FCSTD DOCUMENT  (FreeCAD 1.0R39319 (Git))
Label: 01_assembly_frame
License: All rights reserved
LicenseURL: http://en.wikipedia.org/wiki/All_rights_reserved
objects: App::Link×7, App::FeaturePython×7, Assembly::JointGroup×1, Assembly::AssemblyObject×1
EXTERNAL_REF file=02_frame_15_x_30.FCStd obj=Body
EXTERNAL_REF file=03_frame_sleeve.FCStd obj=Body

FEATURE [App::Link] Body
  LinkedObject = -> <external 02_frame_15_x_30.FCStd>#Body
FEATURE [App::FeaturePython] GroundedJoint  # Assembly grounded joint (typed FeaturePython)
  ObjectToGround = -> Body
FEATURE [App::Link] Body001
  LinkPlacement = pos=(230,-210,15) rot=(1,0,0;1.5708rad)
  LinkedObject = -> <external 03_frame_sleeve.FCStd>#Body
  Placement = pos=(230,-210,15) rot=(1,0,0;1.5708rad)
FEATURE [App::Link] Body002
  LinkPlacement = pos=(138,-210,15) rot=(1,0,0;1.5708rad)
  LinkedObject = -> <external 03_frame_sleeve.FCStd>#Body
  Placement = pos=(138,-210,15) rot=(1,0,0;1.5708rad)
FEATURE [App::Link] Body003
  LinkPlacement = pos=(46,-210,15) rot=(1,0,0;1.5708rad)
  LinkedObject = -> <external 03_frame_sleeve.FCStd>#Body
  Placement = pos=(46,-210,15) rot=(1,0,0;1.5708rad)
FEATURE [App::Link] Body004
  LinkPlacement = pos=(-46,-210,15) rot=(1,0,0;1.5708rad)
  LinkedObject = -> <external 03_frame_sleeve.FCStd>#Body
  Placement = pos=(-46,-210,15) rot=(1,0,0;1.5708rad)
FEATURE [App::Link] Body005
  LinkPlacement = pos=(-138,-210,15) rot=(1,0,0;1.5708rad)
  LinkedObject = -> <external 03_frame_sleeve.FCStd>#Body
  Placement = pos=(-138,-210,15) rot=(1,0,0;1.5708rad)
FEATURE [App::Link] Body006
  LinkPlacement = pos=(-230,-210,15) rot=(1,0,0;1.5708rad)
  LinkedObject = -> <external 03_frame_sleeve.FCStd>#Body
  Placement = pos=(-230,-210,15) rot=(1,0,0;1.5708rad)
FEATURE [App::FeaturePython] Joint  label="Revolute"  # Assembly joint (typed FeaturePython)
  Activated = true
  AngleMax = 0
  AngleMin = 0
  Detach1 = false
  Detach2 = false
  Distance = 0
  Distance2 = 0
  EnableAngleMax = false
  EnableAngleMin = false
  EnableLengthMax = false
  EnableLengthMin = false
  JointType = 1 (Revolute)
  LengthMax = 0
  LengthMin = 0
  Placement1 = pos=(0,0,15) rot=(0,0,1;0rad)
  Placement2 = pos=(0,-225,0) rot=(0.707107,0,0.707107;3.14159rad)
  Reference1 = -> Assembly [Body006.Edge3,Body006.Edge3]
  Reference2 = -> Assembly [Body.Edge26,Body.Edge26]
FEATURE [App::FeaturePython] Joint001  label="Revolute001"  # Assembly joint (typed FeaturePython)
  Activated = true
  AngleMax = 0
  AngleMin = 0
  Detach1 = false
  Detach2 = false
  Distance = 0
  Distance2 = 0
  EnableAngleMax = false
  EnableAngleMin = false
  EnableLengthMax = false
  EnableLengthMin = false
  JointType = 1 (Revolute)
  LengthMax = 0
  LengthMin = 0
  Placement1 = pos=(0,0,15) rot=(0,0,1;0rad)
  Placement2 = pos=(-289.5,-15,0) rot=(-0.707107,0,0.707107;3.14159rad)
  Reference1 = -> Assembly [Body005.Edge3,Body005.Edge3]
  Reference2 = -> Assembly [Body.Edge27,Body.Edge27]
FEATURE [App::FeaturePython] Joint002  label="Revolute002"  # Assembly joint (typed FeaturePython)
  Activated = true
  AngleMax = 0
  AngleMin = 0
  Detach1 = false
  Detach2 = false
  Distance = 0
  Distance2 = 0
  EnableAngleMax = false
  EnableAngleMin = false
  EnableLengthMax = false
  EnableLengthMin = false
  JointType = 1 (Revolute)
  LengthMax = 0
  LengthMin = 0
  Placement1 = pos=(0,0,15) rot=(0,0,1;0rad)
  Placement2 = pos=(0,-210,0) rot=(0.707107,0,0.707107;3.14159rad)
  Reference1 = -> Assembly [Body004.Edge3,Body004.Edge3]
  Reference2 = -> Assembly [Body.Edge28,Body.Edge28]
FEATURE [App::FeaturePython] Joint003  label="Revolute003"  # Assembly joint (typed FeaturePython)
  Activated = true
  AngleMax = 0
  AngleMin = 0
  Detach1 = false
  Detach2 = false
  Distance = 0
  Distance2 = 0
  EnableAngleMax = false
  EnableAngleMin = false
  EnableLengthMax = false
  EnableLengthMin = false
  JointType = 1 (Revolute)
  LengthMax = 0
  LengthMin = 0
  Placement1 = pos=(0,0,15) rot=(0,0,1;0rad)
  Placement2 = pos=(282,0,0) rot=(0.57735,0.57735,0.57735;4.18879rad)
  Reference1 = -> Assembly [Body003.Edge3,Body003.Edge3]
  Reference2 = -> Assembly [Body.Edge29,Body.Edge29]
FEATURE [App::FeaturePython] Joint004  label="Revolute004"  # Assembly joint (typed FeaturePython)
  Activated = true
  AngleMax = 0
  AngleMin = 0
  Detach1 = false
  Detach2 = false
  Distance = 0
  Distance2 = 0
  EnableAngleMax = false
  EnableAngleMin = false
  EnableLengthMax = false
  EnableLengthMin = false
  JointType = 1 (Revolute)
  LengthMax = 0
  LengthMin = 0
  Placement1 = pos=(0,0,15) rot=(0,0,1;0rad)
  Placement2 = pos=(0,210,0) rot=(-0.707107,0,0.707107;3.14159rad)
  Reference1 = -> Assembly [Body002.Edge3,Body002.Edge3]
  Reference2 = -> Assembly [Body.Edge30,Body.Edge30]
FEATURE [App::FeaturePython] Joint005  label="Revolute005"  # Assembly joint (typed FeaturePython)
  Activated = true
  AngleMax = 0
  AngleMin = 0
  Detach1 = false
  Detach2 = false
  Distance = 0
  Distance2 = 0
  EnableAngleMax = false
  EnableAngleMin = false
  EnableLengthMax = false
  EnableLengthMin = false
  JointType = 1 (Revolute)
  LengthMax = 0
  LengthMin = 0
  Placement1 = pos=(0,0,15) rot=(0,0,1;0rad)
  Placement2 = pos=(-289.5,15,0) rot=(-0.707107,0,0.707107;3.14159rad)
  Reference1 = -> Assembly [Body001.Edge3,Body001.Edge3]
  Reference2 = -> Assembly [Body.Edge31,Body.Edge31]
FEATURE [Assembly::JointGroup] Joints
  Group = -> [GroundedJoint,Joint,Joint001,Joint002,Joint003,Joint004,Joint005]
FEATURE [Assembly::AssemblyObject] Assembly
  Group = -> [Joints,Body,GroundedJoint,Body001,Body002,Body003,Body004,Body005,Body006,Joint,Joint001,Joint002,Joint003,Joint004,Joint005]
  Origin = -> Origin
  Type = Assembly

RESOLVED EXTERNAL PARTS (link-assembly join: the EXTERNAL_REF files above that resolve inside this repo's crawl, each included once):
---- part 02_frame_15_x_30.FCStd = doc fcstd_6e40d2458701 ----
FCSTD DOCUMENT  (FreeCAD 1.0R39319 (Git))
Label: 02_frame_15_x_30
License: All rights reserved
LicenseURL: http://en.wikipedia.org/wiki/All_rights_reserved
objects: TechDraw::DrawViewDimension×20, TechDraw::DrawViewBalloon×9, Sketcher::SketchObject×5, TechDraw::DrawProjGroupItem×5, PartDesign::Pocket×4, TechDraw::DrawViewAnnotation×2, Spreadsheet::Sheet×1, PartDesign::Pad×1, PartDesign::Chamfer×1, PartDesign::Body×1, TechDraw::DrawSVGTemplate×1, TechDraw::DrawProjGroup×1, TechDraw::DrawPage×1
note: 59 computed .brp shape members not serialized (recipe doc carries the construction recipe); baked Part::Feature solids carry a one-line shape summary decoded from their .brp

FEATURE [Sketcher::SketchObject] Sketch
  ArcFitTolerance = 1e-06
  AttachmentSupport = -> [XY_Plane]
  FullyConstrained = true
  MakeInternals = false
  MapMode = 5
  expr: Constraints[22] = Spreadsheet.height_outside
  expr: Constraints[23] = Spreadsheet.lenght_outside
  expr: Constraints[24] = Spreadsheet.lenght_outside - 2 * Spreadsheet.height_frame
  expr: Constraints[25] = Spreadsheet.height_outside - 2 * Spreadsheet.height_frame
  sketch-geometry (10):
    g0: LineSegment StartX=-282 StartY=210 StartZ=0 EndX=-282 EndY=-210 EndZ=0
    g1: LineSegment StartX=-282 StartY=-210 StartZ=0 EndX=282 EndY=-210 EndZ=0
    g2: LineSegment StartX=282 StartY=-210 StartZ=0 EndX=282 EndY=210 EndZ=0
    g3: LineSegment StartX=282 StartY=210 StartZ=0 EndX=-282 EndY=210 EndZ=0
    g4: LineSegment [constr] StartX=-282 StartY=210 StartZ=0 EndX=282 EndY=-210 EndZ=0
    g5: LineSegment StartX=-297 StartY=225 StartZ=0 EndX=-297 EndY=-225 EndZ=0
    g6: LineSegment StartX=-297 StartY=-225 StartZ=0 EndX=297 EndY=-225 EndZ=0
    g7: LineSegment StartX=297 StartY=-225 StartZ=0 EndX=297 EndY=225 EndZ=0
    g8: LineSegment StartX=297 StartY=225 StartZ=0 EndX=-297 EndY=225 EndZ=0
    g9: LineSegment [constr] StartX=-297 StartY=225 StartZ=0 EndX=297 EndY=-225 EndZ=0
  constraints (26):
    c: Coincident(g0,g1)
    c: Coincident(g1,g2)
    c: Coincident(g2,g3)
    c: Coincident(g3,g0)
    c: Vertical(g0)
    c: Vertical(g2)
    c: Horizontal(g1)
    c: Horizontal(g3)
    c: Coincident(g4,g0)
    c: Coincident(g4,g1)
    c: Symmetric(g0,g1,g-1)
    c: Coincident(g5,g6)
    c: Coincident(g6,g7)
    c: Coincident(g7,g8)
    c: Coincident(g8,g5)
    c: Vertical(g5)
    c: Vertical(g7)
    c: Horizontal(g6)
    c: Horizontal(g8)
    c: Coincident(g9,g5)
    c: Coincident(g9,g6)
    c: Symmetric(g5,g6,g-1)
    c: DistanceY(g5,g5) = 450
    c: DistanceX(g8,g8) = 594
    c: DistanceX(g3,g3) = 564
    c: DistanceY(g0,g0) = 420
FEATURE [Spreadsheet::Sheet] Spreadsheet
  cells = A2='lenght_outside; B2(lenght_outside)=594; A3='height_outside; B3(height_outside)=450; A5='width_frame; B5(width_frame)=30; A6='height_frame; B6(height_frame)=15; A7='drill_size; B7(drillsize)=81
FEATURE [PartDesign::Pad] Pad
  Direction = (0,0,1)
  Length = 30
  Length2 = 10
  Profile = -> Sketch
  ReferenceAxis = -> Sketch [N_Axis]
  Suppressed = false
  Type = 0
  expr: Length = Spreadsheet.width_frame
FEATURE [Sketcher::SketchObject] Sketch001
  ArcFitTolerance = 1e-06
  AttachmentSupport = -> [YZ_Plane]
  FullyConstrained = true
  MakeInternals = false
  MapMode = 5
  Placement = pos=(0,0,0) rot=(0.57735,0.57735,0.57735;2.0944rad)
  sketch-geometry (4):
    g0: LineSegment StartX=-15 StartY=13 StartZ=0 EndX=-15 EndY=0 EndZ=0
    g1: LineSegment StartX=-15 StartY=0 StartZ=0 EndX=15 EndY=0 EndZ=0
    g2: LineSegment StartX=15 StartY=0 StartZ=0 EndX=15 EndY=13 EndZ=0
    g3: LineSegment StartX=15 StartY=13 StartZ=0 EndX=-15 EndY=13 EndZ=0
  constraints (11):
    c: Coincident(g0,g1)
    c: Coincident(g1,g2)
    c: Coincident(g2,g3)
    c: Coincident(g3,g0)
    c: Vertical(g0)
    c: Vertical(g2)
    c: Horizontal(g1)
    c: Symmetric(g0,g2,g-2)
    c: Horizontal(g1,g-1)
    c: DistanceX(g3,g3) = 30
    c: DistanceY(g0,g0) = 13
FEATURE [PartDesign::Pocket] Pocket
  BaseFeature = -> Pad
  Direction = (-1,0,0)
  Length = 594
  Length2 = 5
  Profile = -> Sketch001
  ReferenceAxis = -> Sketch001 [N_Axis]
  Suppressed = false
  Type = 0
  expr: Length = Spreadsheet.lenght_outside
FEATURE [Sketcher::SketchObject] Sketch002
  ArcFitTolerance = 1e-06
  AttachmentSupport = -> [XZ_Plane]
  ExternalGeometry = -> [Pocket]
  FullyConstrained = true
  MakeInternals = false
  MapMode = 5
  Placement = pos=(0,0,0) rot=(1,0,0;1.5708rad)
  sketch-geometry (7):
    g0: LineSegment [constr] StartX=-282 StartY=15 StartZ=0 EndX=282 EndY=15 EndZ=0
    g1: Circle CenterX=-230 CenterY=15 CenterZ=0 NormalX=0 NormalY=0 NormalZ=1 AngleXU=0 Radius=5
    g2: Circle CenterX=-138 CenterY=15 CenterZ=0 NormalX=0 NormalY=0 NormalZ=1 AngleXU=0 Radius=5
    g3: Circle CenterX=-46 CenterY=15 CenterZ=0 NormalX=0 NormalY=0 NormalZ=1 AngleXU=0 Radius=5
    g4: Circle CenterX=46 CenterY=15 CenterZ=0 NormalX=0 NormalY=0 NormalZ=1 AngleXU=0 Radius=5
    g5: Circle CenterX=138 CenterY=15 CenterZ=0 NormalX=0 NormalY=0 NormalZ=1 AngleXU=0 Radius=5
    g6: Circle CenterX=230 CenterY=15 CenterZ=0 NormalX=0 NormalY=0 NormalZ=1 AngleXU=0 Radius=5
  constraints (23):
    c: Symmetric(g-5,g-5,g0)
    c: Symmetric(g-6,g-6,g0)
    c: DistanceX(g-3,g-3) = 564
    c: PointOnObject(g1,g0)
    c: Diameter(g1) = 10
    c: PointOnObject(g2,g0)
    c: PointOnObject(g3,g0)
    c: PointOnObject(g4,g0)
    c: PointOnObject(g5,g0)
    c: Equal(g1,g2)
    c: Equal(g1,g3)
    c: Equal(g1,g4)
    c: Equal(g5,g1)
    c: PointOnObject(g6,g0)
    c: Equal(g1,g6)
    c: DistanceX(g0,g1) = 52
    c: DistanceX(g6,g0) = 52
    c: DistanceX(g1,g6) = 460
    c: DistanceX(g1,g2) = 92
    c: DistanceX(g2,g3) = 92
    c: DistanceX(g3,g4) = 92
    c: DistanceX(g4,g5) = 92
    c: DistanceX(g5,g6) = 92
FEATURE [PartDesign::Pocket] Pocket001
  BaseFeature = -> Pocket
  Direction = (0,1,-2e-16)
  Length = 225
  Length2 = 5
  Profile = -> Sketch002
  ReferenceAxis = -> Sketch002 [N_Axis]
  Reversed = true
  Suppressed = false
  Type = 0
  expr: Length = Spreadsheet.height_outside / 2
FEATURE [Sketcher::SketchObject] Sketch003
  ArcFitTolerance = 1e-06
  AttachmentSupport = -> [XZ_Plane]
  ExternalGeometry = -> [Pocket001]
  FullyConstrained = true
  MakeInternals = false
  MapMode = 5
  Placement = pos=(0,0,0) rot=(1,0,0;1.5708rad)
  sketch-geometry (7):
    g0: LineSegment [constr] StartX=-282 StartY=15 StartZ=0 EndX=282 EndY=15 EndZ=0
    g1: Circle CenterX=-230 CenterY=15 CenterZ=0 NormalX=0 NormalY=0 NormalZ=1 AngleXU=0 Radius=2.05
    g2: Circle CenterX=-138 CenterY=15 CenterZ=0 NormalX=0 NormalY=0 NormalZ=1 AngleXU=0 Radius=2.05
    g3: Circle CenterX=-46 CenterY=15 CenterZ=0 NormalX=0 NormalY=0 NormalZ=1 AngleXU=0 Radius=2.05
    g4: Circle CenterX=46 CenterY=15 CenterZ=0 NormalX=0 NormalY=0 NormalZ=1 AngleXU=0 Radius=2.05
    g5: Circle CenterX=138 CenterY=15 CenterZ=0 NormalX=0 NormalY=0 NormalZ=1 AngleXU=0 Radius=2.05
    g6: Circle CenterX=230 CenterY=15 CenterZ=0 NormalX=0 NormalY=0 NormalZ=1 AngleXU=0 Radius=2.05
  constraints (22):
    c: Horizontal(g0)
    c: PointOnObject(g0,g-4)
    c: Symmetric(g-3,g-3,g0)
    c: PointOnObject(g1,g0)
    c: Distance(g1,g-3) = 52
    c: Diameter(g1) = 4.1
    c: PointOnObject(g2,g0)
    c: DistanceX(g1,g2) = 92
    c: Equal(g1,g2)
    c: PointOnObject(g3,g0)
    c: Equal(g2,g3)
    c: PointOnObject(g4,g0)
    c: PointOnObject(g5,g0)
    c: Equal(g1,g4)
    c: Equal(g1,g5)
    c: DistanceX(g2,g3) = 92
    c: DistanceX(g3,g4) = 92
    c: DistanceX(g4,g5) = 92
    c: PointOnObject(g6,g0)
    c: Equal(g1,g6)
    c: DistanceX(g5,g6) = 92
    c: DistanceX(g6,g0) = 52
FEATURE [PartDesign::Pocket] Pocket002
  BaseFeature = -> Pocket001
  Direction = (0,1,-2e-16)
  Length = 218
  Length2 = 5
  Profile = -> Sketch003
  ReferenceAxis = -> Sketch003 [N_Axis]
  Suppressed = false
  Type = 0
  expr: Length = Spreadsheet.height_outside / 2 - 7
FEATURE [Sketcher::SketchObject] Sketch004
  ArcFitTolerance = 1e-06
  AttachmentSupport = -> [YZ_Plane]
  ExternalGeometry = -> [Pocket002]
  FullyConstrained = true
  MakeInternals = false
  MapMode = 5
  Placement = pos=(0,0,0) rot=(0.57735,0.57735,0.57735;2.0944rad)
  sketch-geometry (3):
    g0: LineSegment [constr] StartX=-210 StartY=15 StartZ=0 EndX=210 EndY=15 EndZ=0
    g1: Circle CenterX=-170 CenterY=15 CenterZ=0 NormalX=0 NormalY=0 NormalZ=1 AngleXU=0 Radius=2.5
    g2: Circle CenterX=170 CenterY=15 CenterZ=0 NormalX=0 NormalY=0 NormalZ=1 AngleXU=0 Radius=2.5
  constraints (8):
    c: Symmetric(g-3,g-3,g0)
    c: Symmetric(g-4,g-4,g0)
    c: PointOnObject(g1,g0)
    c: PointOnObject(g2,g0)
    c: Distance(g1,g-3) = 40
    c: Distance(g0,g2) = 40
    c: Diameter(g1) = 5
    c: Equal(g1,g2)
FEATURE [PartDesign::Pocket] Pocket003
  BaseFeature = -> Pocket002
  Direction = (-1,0,0)
  Length = 5
  Length2 = 5
  Midplane = true
  Profile = -> Sketch004
  ReferenceAxis = -> Sketch004 [N_Axis]
  Suppressed = false
  Type = 1
FEATURE [PartDesign::Chamfer] Chamfer
  Angle = 45
  Base = -> Pocket003 [Edge41,Edge43,Edge57,Edge58]
  BaseFeature = -> Pocket003
  ChamferType = 0
  FlipDirection = false
  Size = 5
  Size2 = 1
  SupportTransform = false
  Suppressed = false
  UseAllEdges = false
FEATURE [PartDesign::Body] Body
  AllowCompound = false
  Group = -> [Sketch,Pad,Sketch001,Pocket,Sketch002,Pocket001,Sketch003,Pocket002,Sketch004,Pocket003,Chamfer]
  Origin = -> Origin
  Tip = -> Chamfer
FEATURE [TechDraw::DrawSVGTemplate] Template
  EditableTexts = AuthorName=Matthias Mosimann; CheckDate=N/A; CreationDate=15/04/2026; DrawingNumber=1.0; FC-Title=Rahmen; SheetNumber=1 / 1; SupervisorName=N/A; Weight=WEIGHT; scale=1 : 5
  Height = 297
  Orientation = 1
  Template = C:/Program Files/FreeCAD 1.0/data/Mod/TechDraw/Templates/A3_Landscape_TD.svg
  Width = 420
FEATURE [TechDraw::DrawProjGroupItem] View  label="Front"
  CoarseView = false
  Direction = (0,-1,0)
  Focus = 100
  HardHidden = false
  IsoCount = 0
  IsoHidden = false
  IsoVisible = false
  LockPosition = true
  Perspective = false
  Rotation = 0
  RotationVector = (1,0,0)
  Scale = 0.2
  ScaleType = 2
  ScrubCount = 1
  SeamHidden = false
  SeamVisible = true
  SmoothHidden = false
  SmoothVisible = true
  Source = -> [Body]
  Type = 0
  X = 0
  XDirection = (-1,0,-1e-16)
  Y = 0
FEATURE [TechDraw::DrawProjGroupItem] ProjItem  label="Right"
  CoarseView = false
  Direction = (-1,-1e-16,-1e-16)
  Focus = 100
  HardHidden = false
  IsoCount = 0
  IsoHidden = false
  IsoVisible = false
  LockPosition = true
  Perspective = false
  Rotation = 0
  RotationVector = (1,0,0)
  Scale = 0.2
  ScaleType = 2
  ScrubCount = 1
  SeamHidden = false
  SeamVisible = true
  SmoothHidden = false
  SmoothVisible = true
  Source = -> [Body]
  Type = 2
  X = -119.062
  XDirection = (-1e-16,1,0)
  Y = 0
FEATURE [TechDraw::DrawProjGroupItem] ProjItem002  label="Top"
  CoarseView = false
  Direction = (1e-16,0,-1)
  Focus = 100
  HardHidden = true
  IsoCount = 0
  IsoHidden = false
  IsoVisible = false
  LockPosition = true
  Perspective = false
  Rotation = 0
  RotationVector = (1,0,0)
  Scale = 0.2
  ScaleType = 2
  ScrubCount = 1
  SeamHidden = false
  SeamVisible = true
  SmoothHidden = false
  SmoothVisible = true
  Source = -> [Body]
  Type = 4
  X = 0
  XDirection = (-1,0,-1e-16)
  Y = -80.6268
FEATURE [TechDraw::DrawProjGroupItem] ProjItem003  label="Left"
  CoarseView = false
  Direction = (1,-1e-16,1e-16)
  Focus = 100
  HardHidden = false
  IsoCount = 0
  IsoHidden = false
  IsoVisible = false
  LockPosition = true
  Perspective = false
  Rotation = 0
  RotationVector = (1,0,0)
  Scale = 0.2
  ScaleType = 2
  ScrubCount = 1
  SeamHidden = false
  SeamVisible = true
  SmoothHidden = false
  SmoothVisible = true
  Source = -> [Body]
  Type = 1
  X = 121.888
  XDirection = (-1e-16,-1,0)
  Y = 0
FEATURE [TechDraw::DrawProjGroupItem] ProjItem004  label="FrontTopLeft"
  CoarseView = false
  Direction = (0.57735,-0.57735,-0.57735)
  Focus = 100
  HardHidden = false
  IsoCount = 0
  IsoHidden = false
  IsoVisible = false
  LockPosition = true
  Perspective = false
  Rotation = 0
  RotationVector = (1,0,0)
  Scale = 0.2
  ScaleType = 2
  ScrubCount = 1
  SeamHidden = false
  SeamVisible = true
  SmoothHidden = false
  SmoothVisible = true
  Source = -> [Body]
  Type = 6
  X = 147.596
  XDirection = (-0.707107,-0.707107,-1e-16)
  Y = -76.8368
FEATURE [TechDraw::DrawProjGroup] ProjGroup
  Anchor = -> View
  AutoDistribute = true
  LockPosition = false
  ProjectionType = 0
  Rotation = 0
  Scale = 0.2
  ScaleType = 2
  Source = -> [Body]
  Views = -> [View,ProjItem,ProjItem002,ProjItem003,ProjItem004]
  X = 185.522
  Y = 222.445
  spacingX = 15
  spacingY = 15
FEATURE [TechDraw::DrawViewDimension] Dimension
  AngleOverride = false
  Arbitrary = false
  ArbitraryTolerances = false
  BoxCorners = (2) [(-59.4,-45,0),(59.4,45,0)]
  EqualTolerance = true
  ExtensionAngle = 0
  FormatSpec = %.2w
  FormatSpecOverTolerance = %+.2w
  FormatSpecUnderTolerance = %+.2w
  Inverted = false
  LineAngle = 0
  LockPosition = false
  MeasureType = 1
  OverTolerance = 0
  References2D = -> [ProjItem002]
  Rotation = 0
  ScaleType = 0
  TheoreticalExact = false
  Type = 2
  UnderTolerance = 0
  X = -72.114
  Y = 5.93997
FEATURE [TechDraw::DrawViewDimension] Dimension001
  AngleOverride = false
  Arbitrary = false
  ArbitraryTolerances = false
  BoxCorners = (2) [(-59.4,-45,0),(59.4,45,0)]
  EqualTolerance = true
  ExtensionAngle = 0
  FormatSpec = %.2w
  FormatSpecOverTolerance = %+.2w
  FormatSpecUnderTolerance = %+.2w
  Inverted = false
  LineAngle = 0
  LockPosition = false
  MeasureType = 1
  OverTolerance = 0
  References2D = -> [ProjItem002]
  Rotation = 0
  ScaleType = 0
  TheoreticalExact = false
  Type = 1
  UnderTolerance = 0
  X = 0
  Y = 61.892
FEATURE [TechDraw::DrawViewDimension] Dimension002
  AngleOverride = false
  Arbitrary = false
  ArbitraryTolerances = false
  BoxCorners = (2) [(-45,-3,0),(45,3,0)]
  EqualTolerance = true
  ExtensionAngle = 0
  FormatSpec = %.2w
  FormatSpecOverTolerance = %+.2w
  FormatSpecUnderTolerance = %+.2w
  Inverted = false
  LineAngle = 0
  LockPosition = false
  MeasureType = 1
  OverTolerance = 0
  References2D = -> [ProjItem]
  Rotation = 0
  ScaleType = 0
  TheoreticalExact = false
  Type = 0
  UnderTolerance = 0
  X = -39.5
  Y = -15.8335
FEATURE [TechDraw::DrawViewDimension] Dimension003
  AngleOverride = false
  Arbitrary = false
  ArbitraryTolerances = false
  BoxCorners = (2) [(-45,-3,0),(45,3,0)]
  EqualTolerance = true
  ExtensionAngle = 0
  FormatSpec = ⌀%.2w
  FormatSpecOverTolerance = %+.2w
  FormatSpecUnderTolerance = %+.2w
  Inverted = false
  LineAngle = 0
  LockPosition = false
  MeasureType = 1
  OverTolerance = 0
  References2D = -> [ProjItem]
  Rotation = 0
  ScaleType = 0
  TheoreticalExact = false
  Type = 5
  UnderTolerance = 0
  X = -30.7122
  Y = 14.8466
FEATURE [TechDraw::DrawViewDimension] Dimension004
  AngleOverride = false
  Arbitrary = false
  ArbitraryTolerances = false
  BoxCorners = (2) [(-45,-3,0),(45,3,0)]
  EqualTolerance = true
  ExtensionAngle = 0
  FormatSpec = %.2w
  FormatSpecOverTolerance = %+.2w
  FormatSpecUnderTolerance = %+.2w
  Inverted = false
  LineAngle = 0
  LockPosition = false
  MeasureType = 1
  OverTolerance = 0
  References2D = -> [ProjItem]
  Rotation = 0
  ScaleType = 0
  TheoreticalExact = false
  Type = 0
  UnderTolerance = 0
  X = 39.5
  Y = -15.8335
FEATURE [TechDraw::DrawViewDimension] Dimension005
  AngleOverride = false
  Arbitrary = false
  ArbitraryTolerances = false
  BoxCorners = (2) [(-45,-3,0),(45,3,0)]
  EqualTolerance = true
  ExtensionAngle = 0
  FormatSpec = ⌀%.2w
  FormatSpecOverTolerance = %+.2w
  FormatSpecUnderTolerance = %+.2w
  Inverted = false
  LineAngle = 0
  LockPosition = false
  MeasureType = 1
  OverTolerance = 0
  References2D = -> [ProjItem]
  Rotation = 0
  ScaleType = 0
  TheoreticalExact = false
  Type = 5
  UnderTolerance = 0
  X = 38.1595
  Y = 15.5364
FEATURE [TechDraw::DrawViewDimension] Dimension006
  AngleOverride = false
  Arbitrary = false
  ArbitraryTolerances = false
  BoxCorners = (2) [(-45,-3,0),(45,3,0)]
  EqualTolerance = true
  ExtensionAngle = 0
  FormatSpec = %.2w
  FormatSpecOverTolerance = %+.2w
  FormatSpecUnderTolerance = %+.2w
  Inverted = false
  LineAngle = 0
  LockPosition = false
  MeasureType = 1
  OverTolerance = 0
  References2D = -> [ProjItem]
  Rotation = 0
  ScaleType = 0
  TheoreticalExact = false
  Type = 0
  UnderTolerance = 0
  X = -13.9563
  Y = 10.1442
FEATURE [TechDraw::DrawViewDimension] Dimension007
  AngleOverride = false
  Arbitrary = false
  ArbitraryTolerances = false
  BoxCorners = (2) [(-45,-3,0),(45,3,0)]
  EqualTolerance = true
  ExtensionAngle = 0
  FormatSpec = %.2w
  FormatSpecOverTolerance = %+.2w
  FormatSpecUnderTolerance = %+.2w
  Inverted = false
  LineAngle = 0
  LockPosition = false
  MeasureType = 1
  OverTolerance = 0
  References2D = -> [ProjItem]
  Rotation = 0
  ScaleType = 0
  TheoreticalExact = false
  Type = 0
  UnderTolerance = 0
  X = -17.7771
  Y = 24.7768
FEATURE [TechDraw::DrawViewDimension] Dimension008
  AngleOverride = false
  Arbitrary = false
  ArbitraryTolerances = false
  BoxCorners = (2) [(-59.4,-3,0),(59.4,3,0)]
  EqualTolerance = true
  ExtensionAngle = 0
  FormatSpec = %.2w
  FormatSpecOverTolerance = %+.2w
  FormatSpecUnderTolerance = %+.2w
  Inverted = false
  LineAngle = 0
  LockPosition = false
  MeasureType = 1
  OverTolerance = 0
  References2D = -> [View]
  Rotation = 0
  ScaleType = 0
  TheoreticalExact = false
  Type = 0
  UnderTolerance = 0
  X = -52.7
  Y = 22.4873
FEATURE [TechDraw::DrawViewDimension] Dimension009
  AngleOverride = false
  Arbitrary = false
  ArbitraryTolerances = false
  BoxCorners = (2) [(-59.4,-3,0),(59.4,3,0)]
  EqualTolerance = true
  ExtensionAngle = 0
  FormatSpec = %.2w
  FormatSpecOverTolerance = %+.2w
  FormatSpecUnderTolerance = %+.2w
  Inverted = false
  LineAngle = 0
  LockPosition = false
  MeasureType = 1
  OverTolerance = 0
  References2D = -> [View]
  Rotation = 0
  ScaleType = 0
  TheoreticalExact = false
  Type = 1
  UnderTolerance = 0
  X = -36.8
  Y = 22.4873
FEATURE [TechDraw::DrawViewDimension] Dimension010
  AngleOverride = false
  Arbitrary = false
  ArbitraryTolerances = false
  BoxCorners = (2) [(-59.4,-3,0),(59.4,3,0)]
  EqualTolerance = true
  ExtensionAngle = 0
  FormatSpec = %.2w
  FormatSpecOverTolerance = %+.2w
  FormatSpecUnderTolerance = %+.2w
  Inverted = false
  LineAngle = 0
  LockPosition = false
  MeasureType = 1
  OverTolerance = 0
  References2D = -> [View]
  Rotation = 0
  ScaleType = 0
  TheoreticalExact = false
  Type = 2
  UnderTolerance = 0
  X = 65.2162
  Y = 0
FEATURE [TechDraw::DrawViewDimension] Dimension011
  AngleOverride = false
  Arbitrary = false
  ArbitraryTolerances = false
  BoxCorners = (2) [(-59.4,-45,0),(59.4,45,0)]
  EqualTolerance = true
  ExtensionAngle = 0
  FormatSpec = %.2w
  FormatSpecOverTolerance = %+.2w
  FormatSpecUnderTolerance = %+.2w
  Inverted = false
  LineAngle = 0
  LockPosition = false
  MeasureType = 1
  OverTolerance = 0
  References2D = -> [ProjItem002]
  Rotation = 0
  ScaleType = 0
  TheoreticalExact = false
  Type = 0
  UnderTolerance = 0
  X = 62.2692
  Y = 54.4773
FEATURE [TechDraw::DrawViewDimension] Dimension012
  AngleOverride = false
  Arbitrary = false
  ArbitraryTolerances = false
  BoxCorners = (2) [(-59.4,-3,0),(59.4,3,0)]
  EqualTolerance = true
  ExtensionAngle = 0
  FormatSpec = %.2w
  FormatSpecOverTolerance = %+.2w
  FormatSpecUnderTolerance = %+.2w
  Inverted = false
  LineAngle = 0
  LockPosition = false
  MeasureType = 1
  OverTolerance = 0
  References2D = -> [View]
  Rotation = 0
  ScaleType = 0
  TheoreticalExact = false
  Type = 1
  UnderTolerance = 0
  X = -18.4
  Y = 22.4873
FEATURE [TechDraw::DrawViewDimension] Dimension013
  AngleOverride = false
  Arbitrary = false
  ArbitraryTolerances = false
  BoxCorners = (2) [(-59.4,-3,0),(59.4,3,0)]
  EqualTolerance = true
  ExtensionAngle = 0
  FormatSpec = %.2w
  FormatSpecOverTolerance = %+.2w
  FormatSpecUnderTolerance = %+.2w
  Inverted = false
  LineAngle = 0
  LockPosition = false
  MeasureType = 1
  OverTolerance = 0
  References2D = -> [View]
  Rotation = 0
  ScaleType = 0
  TheoreticalExact = false
  Type = 1
  UnderTolerance = 0
  X = 0
  Y = 22.4873
FEATURE [TechDraw::DrawViewDimension] Dimension014
  AngleOverride = false
  Arbitrary = false
  ArbitraryTolerances = false
  BoxCorners = (2) [(-59.4,-3,0),(59.4,3,0)]
  EqualTolerance = true
  ExtensionAngle = 0
  FormatSpec = %.2w
  FormatSpecOverTolerance = %+.2w
  FormatSpecUnderTolerance = %+.2w
  Inverted = false
  LineAngle = 0
  LockPosition = false
  MeasureType = 1
  OverTolerance = 0
  References2D = -> [View]
  Rotation = 0
  ScaleType = 0
  TheoreticalExact = false
  Type = 1
  UnderTolerance = 0
  X = 18.4
  Y = 22.4873
FEATURE [TechDraw::DrawViewDimension] Dimension015
  AngleOverride = false
  Arbitrary = false
  ArbitraryTolerances = false
  BoxCorners = (2) [(-59.4,-3,0),(59.4,3,0)]
  EqualTolerance = true
  ExtensionAngle = 0
  FormatSpec = %.2w
  FormatSpecOverTolerance = %+.2w
  FormatSpecUnderTolerance = %+.2w
  Inverted = false
  LineAngle = 0
  LockPosition = false
  MeasureType = 1
  OverTolerance = 0
  References2D = -> [View]
  Rotation = 0
  ScaleType = 0
  TheoreticalExact = false
  Type = 1
  UnderTolerance = 0
  X = 36.8
  Y = 22.4873
FEATURE [TechDraw::DrawViewDimension] Dimension016
  AngleOverride = false
  Arbitrary = false
  ArbitraryTolerances = false
  BoxCorners = (2) [(-59.4,-3,0),(59.4,3,0)]
  EqualTolerance = true
  ExtensionAngle = 0
  FormatSpec = %.2w
  FormatSpecOverTolerance = %+.2w
  FormatSpecUnderTolerance = %+.2w
  Inverted = false
  LineAngle = 0
  LockPosition = false
  MeasureType = 1
  OverTolerance = 0
  References2D = -> [View]
  Rotation = 0
  ScaleType = 0
  TheoreticalExact = false
  Type = 0
  UnderTolerance = 0
  X = 52.7
  Y = 22.4873
FEATURE [TechDraw::DrawViewAnnotation] Annotation005
  Font = osifont
  LineSpace = 80
  LockPosition = false
  MaxWidth = 100
  Rotation = 0
  Scale = 0.5
  ScaleType = 1
  Text = Rahmen ist aus Flachstahl 30mm x 15mm. | 3D Ansichten können von der angegebenen Skalierungsgrösse abweichen. | Alle Angaben in mm.
  TextSize = 3
  TextStyle = 1
  X = 65.8486
  Y = 170.219
FEATURE [TechDraw::DrawViewBalloon] Balloon
  BubbleShape = 0
  EndType = 0
  EndTypeScale = 1
  KinkLength = 5
  LockPosition = false
  OriginX = -67.1399
  OriginY = 96.7687
  Rotation = 0
  ScaleType = 0
  ShapeScale = 1
  SourceView = -> Annotation005
  Text = 1
  TextWrapLen = -1
  X = -98.1022
  Y = 165.989
FEATURE [TechDraw::DrawViewAnnotation] Annotation
  Font = osifont
  LineSpace = 80
  LockPosition = false
  MaxWidth = 100
  Rotation = 0
  Scale = 0.5
  ScaleType = 1
  Text = (1) Montageloch kann frei gewählt werden im Durchmesser und Platzierung. Wichtig ist dass auf der Innenseite Senkungen passend vorhanden sind. Hier sind nur Beispiele eingezeichnet.   | (2) Unten im Rahmen werden die Edelstahlhülsen mit Sackloch eingeschweist. Bohrung muss ggf. etwas grösser sein als 10mm, damit die Hülse passt. | (3) Oben im Rahmen werden nur die 4.1mm Sacklöcher gebohrt. Ohne Hülsen.
  TextSize = 3
  TextStyle = 0
  X = 65.8486
  Y = 113.793
FEATURE [TechDraw::DrawViewBalloon] Balloon002
  BubbleShape = 0
  EndType = 0
  EndTypeScale = 1
  KinkLength = 5
  LockPosition = false
  OriginX = -225
  OriginY = 0
  Rotation = 0
  ScaleType = 0
  ShapeScale = 1
  SourceView = -> View
  Text = 2
  TextWrapLen = -1
  X = -121.803
  Y = -73.4565
FEATURE [TechDraw::DrawViewBalloon] Balloon003
  BubbleShape = 0
  EndType = 0
  EndTypeScale = 1
  KinkLength = 5
  LockPosition = false
  OriginX = -5.29303
  OriginY = -183.225
  Rotation = 0
  ScaleType = 0
  ShapeScale = 1
  SourceView = -> ProjItem004
  Text = 2
  TextWrapLen = -1
  X = 166.509
  Y = -226.829
FEATURE [TechDraw::DrawViewBalloon] Balloon004
  BubbleShape = 0
  EndType = 0
  EndTypeScale = 1
  KinkLength = 5
  LockPosition = false
  OriginX = -135.95
  OriginY = 0
  Rotation = 0
  ScaleType = 0
  ShapeScale = 1
  SourceView = -> View
  Text = 3
  TextWrapLen = -1
  X = -243.989
  Y = 155.417
FEATURE [TechDraw::DrawViewBalloon] Balloon005
  BubbleShape = 0
  EndType = 0
  EndTypeScale = 1
  KinkLength = 5
  LockPosition = false
  OriginX = -116.686
  OriginY = 105.548
  Rotation = 0
  ScaleType = 0
  ShapeScale = 1
  SourceView = -> ProjItem004
  Text = 3
  TextWrapLen = -1
  X = -266.453
  Y = 203.449
FEATURE [TechDraw::DrawViewBalloon] Balloon006
  BubbleShape = 0
  EndType = 0
  EndTypeScale = 1
  KinkLength = 5
  LockPosition = false
  OriginX = 75.446
  OriginY = 191.023
  Rotation = 0
  ScaleType = 0
  ShapeScale = 1
  SourceView = -> ProjItem004
  Text = 1
  TextWrapLen = -1
  X = 175.446
  Y = 291.023
FEATURE [TechDraw::DrawViewDimension] Dimension017
  AngleOverride = false
  Arbitrary = false
  ArbitraryTolerances = false
  BoxCorners = (2) [(-59.4,-3,0),(59.4,3,0)]
  EqualTolerance = true
  ExtensionAngle = 0
  FormatSpec = ⌀%.2w
  FormatSpecOverTolerance = %+.2w
  FormatSpecUnderTolerance = %+.2w
  Inverted = false
  LineAngle = 0
  LockPosition = false
  MeasureType = 1
  OverTolerance = 0
  References2D = -> [View]
  Rotation = 0
  ScaleType = 0
  TheoreticalExact = true
  Type = 5
  UnderTolerance = 0
  X = -66.349
  Y = -6.38909
FEATURE [TechDraw::DrawViewDimension] Dimension018
  AngleOverride = false
  Arbitrary = false
  ArbitraryTolerances = false
  BoxCorners = (2) [(-59.4,-3,0),(59.4,3,0)]
  EqualTolerance = true
  ExtensionAngle = 0
  FormatSpec = ⌀%.2w
  FormatSpecOverTolerance = %+.2w
  FormatSpecUnderTolerance = %+.2w
  Inverted = false
  LineAngle = 0
  LockPosition = false
  MeasureType = 1
  OverTolerance = 0
  References2D = -> [View]
  Rotation = 0
  ScaleType = 0
  TheoreticalExact = false
  Type = 5
  UnderTolerance = 0
  X = -66.044
  Y = 23.5898
FEATURE [TechDraw::DrawViewDimension] Dimension019
  AngleOverride = false
  Arbitrary = false
  ArbitraryTolerances = false
  BoxCorners = (2) [(-59.4,-45,-1e-07),(59.4,45,1e-07)]
  EqualTolerance = true
  ExtensionAngle = 0
  FormatSpec = %.2w
  FormatSpecOverTolerance = %+.2w
  FormatSpecUnderTolerance = %+.2w
  Inverted = false
  LineAngle = 0
  LockPosition = false
  MeasureType = 1
  OverTolerance = 0
  References2D = -> [ProjItem002]
  Rotation = 0
  ScaleType = 0
  TheoreticalExact = false
  Type = 0
  UnderTolerance = 0
  X = -42.8631
  Y = 50.9888
FEATURE [TechDraw::DrawViewBalloon] Balloon007
  BubbleShape = 0
  EndType = 0
  EndTypeScale = 1
  KinkLength = 5
  LockPosition = false
  OriginX = -232.05
  OriginY = 214
  Rotation = 0
  ScaleType = 0
  ShapeScale = 1
  SourceView = -> ProjItem002
  Text = 3
  TextWrapLen = -1
  X = -331.685
  Y = 266.2
FEATURE [TechDraw::DrawViewBalloon] Balloon008
  BubbleShape = 0
  EndType = 0
  EndTypeScale = 1
  KinkLength = 5
  LockPosition = false
  OriginX = -284.5
  OriginY = 175
  Rotation = 0
  ScaleType = 0
  ShapeScale = 1
  SourceView = -> ProjItem002
  Text = 1
  TextWrapLen = -1
  X = -390.448
  Y = 196.452
FEATURE [TechDraw::DrawViewBalloon] Balloon009
  BubbleShape = 0
  EndType = 0
  EndTypeScale = 1
  KinkLength = 5
  LockPosition = false
  OriginX = -143
  OriginY = -217.5
  Rotation = 0
  ScaleType = 0
  ShapeScale = 1
  SourceView = -> ProjItem002
  Text = 2
  TextWrapLen = -1
  X = -270.817
  Y = -305.468
FEATURE [TechDraw::DrawPage] Page
  KeepUpdated = true
  NextBalloonIndex = 11
  ProjectionType = 0
  Template = -> Template
  Views = -> [ProjGroup,Dimension,Dimension001,Dimension002,Dimension003,Dimension004,Dimension005,Dimension006,Dimension007,Dimension008,Dimension009,Dimension010,Dimension011,Dimension012,Dimension013,Dimension014,Dimension015,Dimension016,Annotation005,Balloon,Annotation,Balloon002,Balloon003,Balloon004,Balloon005,Balloon006,Dimension017,Dimension018,Dimension019,Balloon007,Balloon008,Balloon009]
---- part 03_frame_sleeve.FCStd = doc fcstd_73df761d6e07 ----
FCSTD DOCUMENT  (FreeCAD 1.0R39319 (Git))
Label: 03_frame_sleeve
License: All rights reserved
LicenseURL: http://en.wikipedia.org/wiki/All_rights_reserved
objects: TechDraw::DrawViewDimension×5, TechDraw::DrawProjGroupItem×4, Sketcher::SketchObject×2, TechDraw::DrawViewAnnotation×2, PartDesign::Pad×1, PartDesign::Pocket×1, PartDesign::Body×1, TechDraw::DrawSVGTemplate×1, TechDraw::DrawProjGroup×1, TechDraw::DrawViewBalloon×1, TechDraw::DrawPage×1
note: 17 computed .brp shape members not serialized (recipe doc carries the construction recipe); baked Part::Feature solids carry a one-line shape summary decoded from their .brp

FEATURE [Sketcher::SketchObject] Sketch
  ArcFitTolerance = 1e-06
  AttachmentSupport = -> [XY_Plane]
  FullyConstrained = true
  MakeInternals = false
  MapMode = 5
  sketch-geometry (1):
    g0: Circle CenterX=0 CenterY=0 CenterZ=0 NormalX=0 NormalY=0 NormalZ=1 AngleXU=0 Radius=5
  constraints (2):
    c: Coincident(g0,g-1)
    c: Diameter(g0) = 10
FEATURE [PartDesign::Pad] Pad
  Direction = (0,0,1)
  Length = 15
  Length2 = 10
  Profile = -> Sketch
  ReferenceAxis = -> Sketch [N_Axis]
  Suppressed = false
  Type = 0
FEATURE [Sketcher::SketchObject] Sketch001
  ArcFitTolerance = 1e-06
  AttachmentSupport = -> [XY_Plane]
  FullyConstrained = true
  MakeInternals = false
  MapMode = 5
  sketch-geometry (1):
    g0: Circle CenterX=0 CenterY=0 CenterZ=0 NormalX=0 NormalY=0 NormalZ=1 AngleXU=0 Radius=2.05
  constraints (2):
    c: Coincident(g0,g-1)
    c: Diameter(g0) = 4.1
FEATURE [PartDesign::Pocket] Pocket
  BaseFeature = -> Pad
  Direction = (0,0,-1)
  Length = 7
  Length2 = 5
  Profile = -> Sketch001
  ReferenceAxis = -> Sketch001 [N_Axis]
  Reversed = true
  Suppressed = false
  Type = 0
FEATURE [PartDesign::Body] Body
  AllowCompound = false
  Group = -> [Sketch,Pad,Sketch001,Pocket]
  Origin = -> Origin
  Tip = -> Pocket
FEATURE [TechDraw::DrawSVGTemplate] Template
  EditableTexts = AuthorName=Matthias Mosimann; CheckDate=N/A; CreationDate=15/04/2026; DrawingNumber=1.0; FC-Title=Hülse für Rahmen; SheetNumber=1 / 1; SupervisorName=N/A; Weight=N/A; scale=2 : 1
  Height = 297
  Orientation = 1
  Template = C:/Program Files/FreeCAD 1.0/data/Mod/TechDraw/Templates/A3_Landscape_TD.svg
  Width = 420
FEATURE [TechDraw::DrawProjGroupItem] View  label="Front"
  CoarseView = false
  Direction = (0,-1,0)
  Focus = 100
  HardHidden = false
  IsoCount = 0
  IsoHidden = false
  IsoVisible = false
  LockPosition = true
  Perspective = false
  Rotation = 0
  RotationVector = (1,0,0)
  Scale = 2
  ScaleType = 2
  ScrubCount = 1
  SeamHidden = false
  SeamVisible = true
  SmoothHidden = false
  SmoothVisible = true
  Source = -> [Body]
  Type = 0
  X = 0
  XDirection = (1,0,0)
  Y = 0
FEATURE [TechDraw::DrawProjGroupItem] ProjItem  label="Left"
  CoarseView = false
  Direction = (-1,-1e-16,0)
  Focus = 100
  HardHidden = true
  IsoCount = 0
  IsoHidden = false
  IsoVisible = false
  LockPosition = true
  Perspective = false
  Rotation = 0
  RotationVector = (1,0,0)
  Scale = 2
  ScaleType = 0
  ScrubCount = 1
  SeamHidden = false
  SeamVisible = true
  SmoothHidden = false
  SmoothVisible = true
  Source = -> [Body]
  Type = 1
  X = 50
  XDirection = (1e-16,-1,0)
  Y = 0
FEATURE [TechDraw::DrawProjGroupItem] ProjItem001  label="Bottom"
  CoarseView = false
  Direction = (0,0,-1)
  Focus = 100
  HardHidden = false
  IsoCount = 0
  IsoHidden = false
  IsoVisible = false
  LockPosition = true
  Perspective = false
  Rotation = 0
  RotationVector = (1,0,0)
  Scale = 2
  ScaleType = 0
  ScrubCount = 1
  SeamHidden = false
  SeamVisible = true
  SmoothHidden = false
  SmoothVisible = true
  Source = -> [Body]
  Type = 5
  X = 0
  XDirection = (1,0,0)
  Y = 55
FEATURE [TechDraw::DrawProjGroupItem] ProjItem002  label="Top"
  CoarseView = false
  Direction = (0,0,1)
  Focus = 100
  HardHidden = false
  IsoCount = 0
  IsoHidden = false
  IsoVisible = false
  LockPosition = true
  Perspective = false
  Rotation = 0
  RotationVector = (1,0,0)
  Scale = 2
  ScaleType = 0
  ScrubCount = 1
  SeamHidden = false
  SeamVisible = true
  SmoothHidden = false
  SmoothVisible = true
  Source = -> [Body]
  Type = 4
  X = 0
  XDirection = (1,0,0)
  Y = -55
FEATURE [TechDraw::DrawProjGroup] ProjGroup
  Anchor = -> View
  AutoDistribute = true
  LockPosition = false
  ProjectionType = 0
  Rotation = 0
  Scale = 2
  ScaleType = 2
  Source = -> [Body]
  Views = -> [View,ProjItem,ProjItem001,ProjItem002]
  X = 150.687
  Y = 158.223
  spacingX = 30
  spacingY = 30
FEATURE [TechDraw::DrawViewDimension] Dimension
  AngleOverride = false
  Arbitrary = false
  ArbitraryTolerances = false
  BoxCorners = (2) [(-10,-10,0),(10,10,0)]
  EqualTolerance = true
  ExtensionAngle = 0
  FormatSpec = ⌀%.2w
  FormatSpecOverTolerance = %+.2w
  FormatSpecUnderTolerance = %+.2w
  Inverted = false
  LineAngle = 0
  LockPosition = false
  MeasureType = 1
  OverTolerance = 0
  References2D = -> [ProjItem001]
  Rotation = 0
  ScaleType = 0
  TheoreticalExact = false
  Type = 5
  UnderTolerance = 0
  X = -46.139
  Y = 8.07909
FEATURE [TechDraw::DrawViewDimension] Dimension001
  AngleOverride = false
  Arbitrary = false
  ArbitraryTolerances = false
  BoxCorners = (2) [(-10,-10,0),(10,10,0)]
  EqualTolerance = true
  ExtensionAngle = 0
  FormatSpec = ⌀%.2w
  FormatSpecOverTolerance = %+.2w
  FormatSpecUnderTolerance = %+.2w
  Inverted = false
  LineAngle = 0
  LockPosition = false
  MeasureType = 1
  OverTolerance = 0
  References2D = -> [ProjItem001]
  Rotation = 0
  ScaleType = 0
  TheoreticalExact = false
  Type = 5
  UnderTolerance = 0
  X = -40.3274
  Y = 19.1595
FEATURE [TechDraw::DrawViewDimension] Dimension002
  AngleOverride = false
  Arbitrary = false
  ArbitraryTolerances = false
  BoxCorners = (2) [(-10,-15,-1e-07),(10,15,1e-07)]
  EqualTolerance = true
  ExtensionAngle = 0
  FormatSpec = %.2w
  FormatSpecOverTolerance = %+.2w
  FormatSpecUnderTolerance = %+.2w
  Inverted = false
  LineAngle = 0
  LockPosition = false
  MeasureType = 1
  OverTolerance = 0
  References2D = -> [ProjItem]
  Rotation = 0
  ScaleType = 0
  TheoreticalExact = false
  Type = 2
  UnderTolerance = 0
  X = 34.4112
  Y = -8
FEATURE [TechDraw::DrawViewDimension] Dimension003
  AngleOverride = false
  Arbitrary = false
  ArbitraryTolerances = false
  BoxCorners = (2) [(-10,-15,-1e-07),(10,15,1e-07)]
  EqualTolerance = true
  ExtensionAngle = 0
  FormatSpec = %.2w
  FormatSpecOverTolerance = %+.2w
  FormatSpecUnderTolerance = %+.2w
  Inverted = false
  LineAngle = 0
  LockPosition = false
  MeasureType = 1
  OverTolerance = 0
  References2D = -> [ProjItem]
  Rotation = 0
  ScaleType = 0
  TheoreticalExact = false
  Type = 2
  UnderTolerance = 0
  X = -27.1693
  Y = 0
FEATURE [TechDraw::DrawViewDimension] Dimension004
  AngleOverride = false
  Arbitrary = false
  ArbitraryTolerances = false
  BoxCorners = (2) [(-10,-15,-1e-07),(10,15,1e-07)]
  EqualTolerance = true
  ExtensionAngle = 0
  FormatSpec = %.2w
  FormatSpecOverTolerance = %+.2w
  FormatSpecUnderTolerance = %+.2w
  Inverted = false
  LineAngle = 0
  LockPosition = false
  MeasureType = 1
  OverTolerance = 0
  References2D = -> [ProjItem]
  Rotation = 0
  ScaleType = 0
  TheoreticalExact = false
  Type = 0
  UnderTolerance = 0
  X = 22.1267
  Y = -26.0991
FEATURE [TechDraw::DrawViewAnnotation] Annotation
  Font = osifont
  LineSpace = 80
  LockPosition = false
  MaxWidth = 120
  Rotation = 0
  Scale = 0.5
  ScaleType = 1
  Text = (1) Hülse hat 7mm Sackloch. damit 9mm Stift aufsteht. Ausserdem hat die Sacklochbohrung 4.1mm Durchmesser, damit die Lamelle frei beweglich ist.
  TextSize = 3
  TextStyle = 0
  X = 330.887
  Y = 151.302
FEATURE [TechDraw::DrawViewBalloon] Balloon
  BubbleShape = 0
  EndType = 0
  EndTypeScale = 1
  KinkLength = 5
  LockPosition = false
  OriginX = 2.05
  OriginY = -4
  Rotation = 0
  ScaleType = 0
  ShapeScale = 1
  SourceView = -> ProjItem
  Text = 1
  TextWrapLen = -1
  X = 12.05
  Y = 6
FEATURE [TechDraw::DrawViewAnnotation] Annotation005
  Font = osifont
  LineSpace = 80
  LockPosition = false
  MaxWidth = 120
  Rotation = 0
  Scale = 0.5
  ScaleType = 1
  Text = Hülse ist aus Edelstahl. | 3D Ansichten können von der angegebenen Skalierungsgrösse abweichen. | Alle Angaben in mm.
  TextSize = 3
  TextStyle = 1
  X = 330.887
  Y = 189.946
FEATURE [TechDraw::DrawPage] Page
  KeepUpdated = true
  NextBalloonIndex = 2
  ProjectionType = 0
  Template = -> Template
  Views = -> [ProjGroup,Dimension,Dimension001,Dimension002,Dimension003,Dimension004,Annotation,Balloon,Annotation005]
